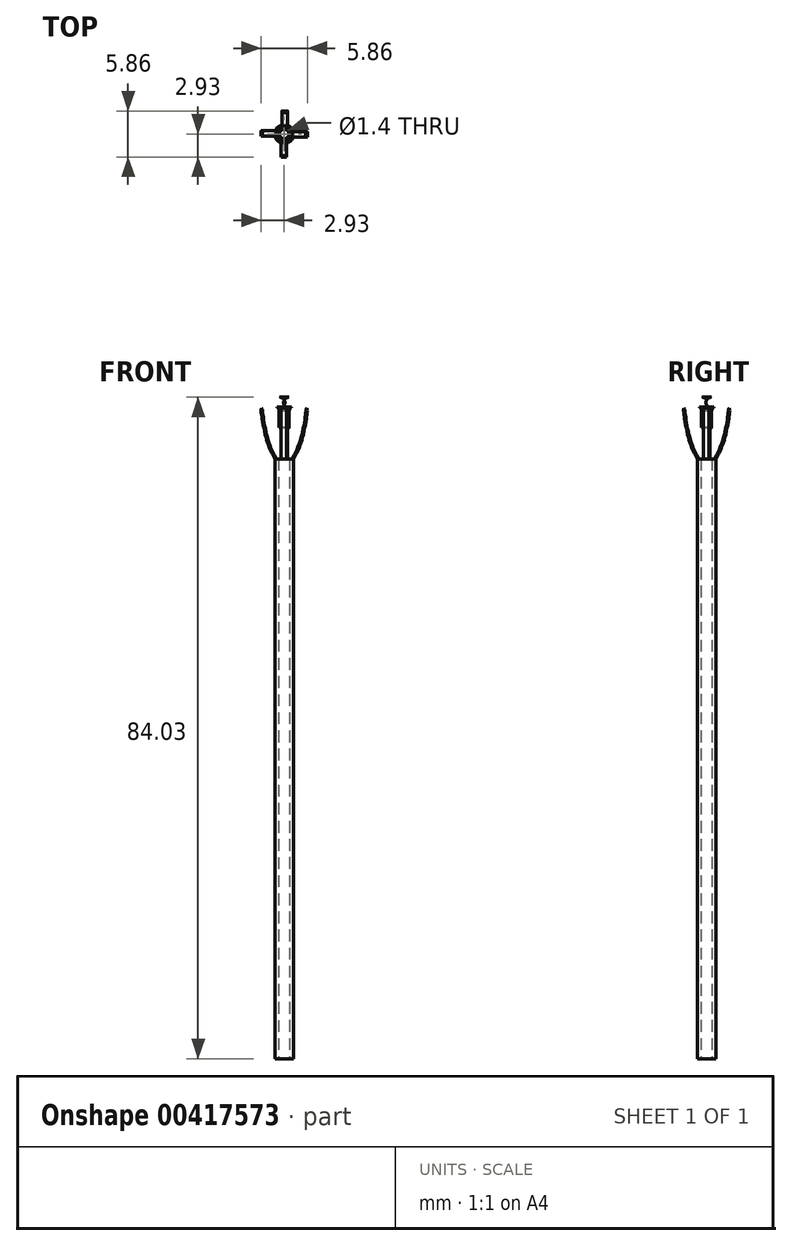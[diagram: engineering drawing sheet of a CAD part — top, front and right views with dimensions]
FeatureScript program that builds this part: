
annotation { "Feature Type Name" : "Feature", "Feature Type Description" : "" }
export const myFeature = defineFeature(function(context is Context, id is Id, definition is map)
    precondition{}
    {
        {
            var Q0;
            Q0=qCreatedBy(makeId("Front.planeOp"),FACE);
            var sketch = newSketch(context, id + "F0", { "sketchPlane" : qUnion([Q0])});
            skLineSegment(sketch, "E0.bottom", {"start": v(-1.2, 0) * mm, "end": v(-0.7, 0) * mm});
            skLineSegment(sketch, "E0.top", {"start": v(-1.2, -76.2) * mm, "end": v(-0.7, -76.2) * mm});
            skLineSegment(sketch, "E0.left", {"start": v(-1.2, 0) * mm, "end": v(-1.2, -76.2) * mm});
            skLineSegment(sketch, "E0.right", {"start": v(-0.7, 0) * mm, "end": v(-0.7, -76.2) * mm});
            skLineSegment(sketch, "E1", {"start": v(0, -108.83) * mm, "end": v(0, 61.19) * mm, "construction": true});
            skSolve(sketch);
        }
        {
            var Q0;
            Q0=makeQuery(id+"F0.imprint","IMPRINT",FACE,{"disambiguationData":[TD([[makeQuery(id+"F0.imprint","IMPRINT",EDGE,{"derivedFrom":sQuery(id+"F0.wireOp",EDGE,"E0.bottom")}),-1.0]])]});
            var Q1;
            Q1=sQuery(id+"F0.wireOp",EDGE,"E1");
            revolve(context, id + "F1", {"entities" : qUnion([Q0]), "axis" : qUnion([Q1]), "revolveType" : RevolveType.FULL});
        }
        {
            var Q0;
            Q0=qCreatedBy(makeId("Front.planeOp"),FACE);
            var sketch = newSketch(context, id + "F2", { "sketchPlane" : qUnion([Q0])});
            skFitSpline(sketch, "E2", {"points": [v(-1.01, 0) * mm, v(-2.13, 2.64) * mm, v(-2.76, 6.14) * mm, v(-2.74, 6.29) * mm], "startDerivative": vector(-2.8, 5.23) * mm, "endDerivative": vector(0.34, 0.95) * mm});
            skSolve(sketch);
        }
        {
            var Q0;
            Q0=makeQuery(id+"F1.opRevolve","SWEPT_FACE",FACE,{"disambiguationData":[OSD([sQuery(id+"F0.wireOp",EDGE,"E0.bottom")])]});
            var sketch = newSketch(context, id + "F3", { "sketchPlane" : qUnion([Q0])});
            skLineSegment(sketch, "E3.bottom", {"start": v(-1, -0.3) * mm, "end": v(-1.2, -0.3) * mm});
            skLineSegment(sketch, "E3.top", {"start": v(-1, 0.42) * mm, "end": v(-1.2, 0.42) * mm});
            skLineSegment(sketch, "E3.left", {"start": v(-1, -0.3) * mm, "end": v(-1, 0.42) * mm});
            skLineSegment(sketch, "E3.right", {"start": v(-1.2, -0.3) * mm, "end": v(-1.2, 0.42) * mm});
            skSolve(sketch);
        }
        {
            var Q0;
            Q0 = qSketchRegion(id + "F3", true);
            var Q1;
            Q1=sQuery(id+"F2.wireOp",EDGE,"E2");
            sweep(context, id + "F4", {"operationType" : NewBodyOperationType.ADD, "profiles" : qUnion([Q0]), "path" : qUnion([Q1])});
        }
        {
            var Q0;
            Q0=qCreatedBy(makeId("Front.planeOp"),FACE);
            var sketch = newSketch(context, id + "F5", { "sketchPlane" : qUnion([Q0])});
            skLineSegment(sketch, "E4", {"start": v(0, 7.31) * mm, "end": v(0, -0.67) * mm, "construction": true});
            skSolve(sketch);
        }
        {
            var Q0;
            Q0=makeQuery(id+"F1.opRevolve","SWEPT_BODY",BODY,{"disambiguationData":[OSD([sQuery(id+"F0.wireOp",EDGE,"E0.bottom"),sQuery(id+"F0.wireOp",EDGE,"E0.top"),sQuery(id+"F0.wireOp",EDGE,"E0.left"),sQuery(id+"F0.wireOp",EDGE,"E0.right")])]});
            var Q1;
            Q1=sQuery(id+"F5.wireOp",EDGE,"E4");
            circularPattern(context, id + "F6", {"operationType" : NewBodyOperationType.ADD, "entities" : qUnion([Q0]), "axis" : qUnion([Q1]), "angle" : 360 * degree, "instanceCount" : 4, "equalSpace" : true});
        }
        {
            var Q0;
            Q0=qCreatedBy(makeId("Front.planeOp"),FACE);
            var sketch = newSketch(context, id + "F7", { "sketchPlane" : qUnion([Q0])});
            skLineSegment(sketch, "E5", {"start": v(0, 14.25) * mm, "end": v(0, -7.67) * mm, "construction": true});
            skLineSegment(sketch, "E6", {"start": v(0, 7.83) * mm, "end": v(-0.6, 7.83) * mm});
            skLineSegment(sketch, "E7", {"start": v(-0.63, 6.11) * mm, "end": v(-0.63, 3.95) * mm});
            skLineSegment(sketch, "E8", {"start": v(-0.63, 3.95) * mm, "end": v(0, 3.95) * mm});
            skLineSegment(sketch, "E9", {"start": v(0, 3.95) * mm, "end": v(0, 7.83) * mm});
            skPoint(sketch, "E10.visualSharp", {"position": v(-0.63, 6.47) * mm});
            skArc(sketch, "E11", {"start": v(-0.6, 7.83) * mm, "mid": v(-1.25, 7.32) * mm, "end": v(-0.92, 6.56) * mm});
            skArc(sketch, "E12", {"start": v(-0.63, 6.11) * mm, "mid": v(-0.73, 6.37) * mm, "end": v(-0.92, 6.56) * mm});
            skPoint(sketch, "E13.orphan", {"position": v(-0.6, 6.47) * mm});
            skSolve(sketch);
        }
        {
            var Q0;
            Q0=makeQuery(id+"F7.imprint","IMPRINT",FACE,{"disambiguationData":[TD([[makeQuery(id+"F7.imprint","IMPRINT",EDGE,{"derivedFrom":sQuery(id+"F7.wireOp",EDGE,"E6")}),1.0]])]});
            var Q1;
            Q1=sQuery(id+"F7.wireOp",EDGE,"E5");
            revolve(context, id + "F8", {"entities" : qUnion([Q0]), "axis" : qUnion([Q1]), "revolveType" : RevolveType.FULL});
        }
    });
